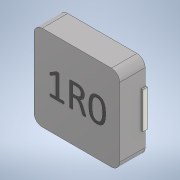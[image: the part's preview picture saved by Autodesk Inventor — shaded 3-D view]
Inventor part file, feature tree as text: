
AUTODESK INVENTOR PART (.ipt)
format: ipt  version: 2020 (Build 240168000, 168)  size: 272,896 bytes
history: native  units: mm
features: extrude x3, sketch x3, fillet x1
ambient origin geometry x8: Origin, YZ Plane, XZ Plane, XY Plane, X Axis, Y Axis, Z Axis, Center Point
bodies: Solid1 (feature_tree)
feature tree (7):
  extrude  "Extrusion1"  Depth=5.2mm
  extrude  "Extrusion2"  Depth=1.2mm
  fillet  "Fillet1"  Radius=0.1mm
  extrude  "Extrusion4"  Depth=5.4mm
  sketch  "Sketch1"  dims[d0=5.2mm d1=5.2mm]
  sketch  "Sketch2"  dims[d2=1.55mm d3=0.0mm d4=1.2mm d5=0.1mm]
  sketch  "Sketch3"  dims[d6=2.2mm d7=5.4mm d8=0.05mm d9=0.0mm d10=0.25mm d11=0.0mm d12=0.5mm d13=5.0mm d14=2.5mm d17=0.01mm d18=0.0mm]
